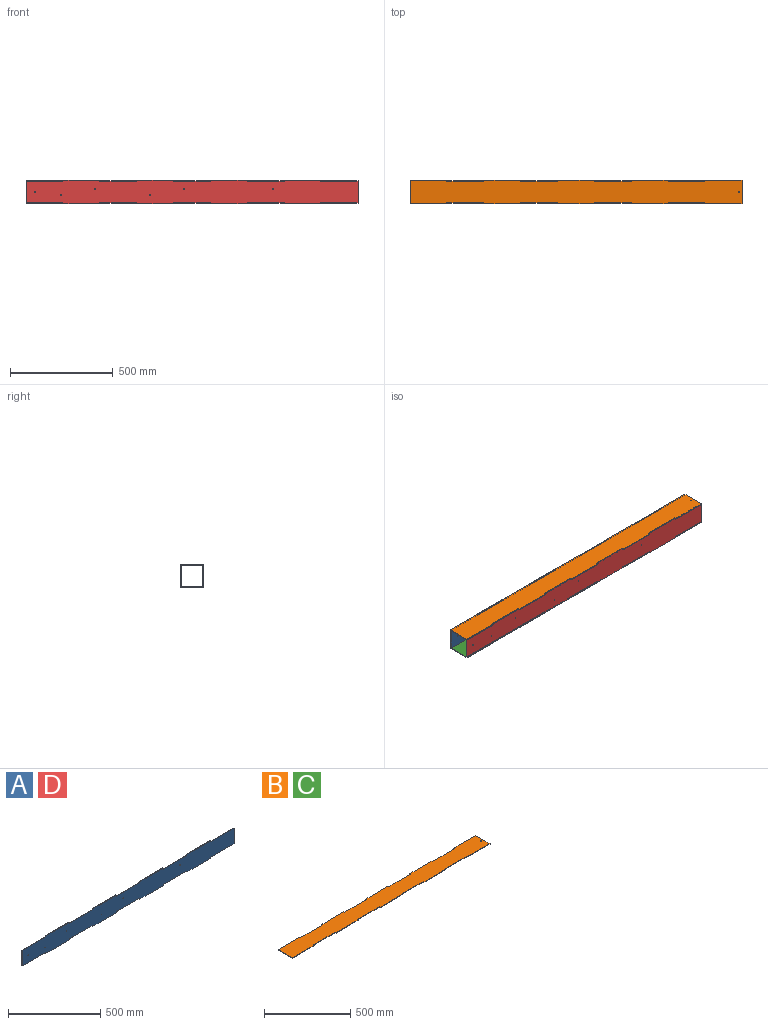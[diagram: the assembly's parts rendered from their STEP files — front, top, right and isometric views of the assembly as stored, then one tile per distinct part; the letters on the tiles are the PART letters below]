
ASSEMBLY  parts=4 mates=9
PART A: 44 faces, bbox 1619.3x3.2x115.9 mm
  f0: plane 103.19x3.18mm, normal (-1,0,0), area 327.6mm2, adj f1,f40,f42,f43
  f1: plane 179.83x3.18mm, normal (0,0,-1), area 571mm2, adj f0,f2,f42,f43
  f2: plane 6.35x3.18mm, normal (-1,0,0), area 20.2mm2, adj f1,f3,f42,f43
  f3: plane 179.83x3.18mm, normal (0,0,-1), area 571mm2, adj f2,f4,f42,f43
  f4: plane 6.35x3.18mm, normal (1,0,0), area 20.2mm2, adj f3,f5,f42,f43
  f5: plane 179.83x3.18mm, normal (0,0,-1), area 571mm2, adj f4,f6,f42,f43
  f6: plane 6.35x3.18mm, normal (-1,0,0), area 20.2mm2, adj f5,f7,f42,f43
  f7: plane 179.83x3.18mm, normal (0,0,-1), area 571mm2, adj f6,f8,f42,f43
  f8: plane 6.35x3.18mm, normal (1,0,0), area 20.2mm2, adj f7,f9,f42,f43
  f9: plane 179.83x3.18mm, normal (0,0,-1), area 571mm2, adj f8,f10,f42,f43
  f10: plane 6.35x3.18mm, normal (-1,0,0), area 20.2mm2, adj f9,f11,f42,f43
  f11: plane 179.83x3.18mm, normal (0,0,-1), area 571mm2, adj f10,f12,f42,f43
  f12: plane 6.35x3.18mm, normal (1,0,0), area 20.2mm2, adj f11,f13,f42,f43
  f13: plane 179.83x3.18mm, normal (0,0,-1), area 571mm2, adj f12,f14,f42,f43
  f14: plane 6.35x3.18mm, normal (-1,0,0), area 20.2mm2, adj f13,f15,f42,f43
  f15: plane 179.83x3.18mm, normal (0,0,-1), area 571mm2, adj f14,f16,f42,f43
  f16: plane 6.35x3.18mm, normal (1,0,0), area 20.2mm2, adj f15,f17,f42,f43
  f17: plane 180.59x3.18mm, normal (0,0,-1), area 573.4mm2, adj f16,f18,f42,f43
  f18: plane 103.19x3.18mm, normal (1,0,0), area 327.6mm2, adj f17,f19,f42,f43
  f19: plane 180.59x3.18mm, normal (0,0,1), area 573.4mm2, adj f18,f20,f42,f43
  f20: plane 6.35x3.18mm, normal (1,0,0), area 20.2mm2, adj f19,f21,f42,f43
  f21: plane 179.83x3.18mm, normal (0,0,1), area 571mm2, adj f20,f22,f42,f43
  f22: plane 6.35x3.18mm, normal (-1,0,0), area 20.2mm2, adj f21,f23,f42,f43
  f23: plane 179.83x3.18mm, normal (0,0,1), area 571mm2, adj f22,f24,f42,f43
  f24: plane 6.35x3.18mm, normal (1,0,0), area 20.2mm2, adj f23,f25,f42,f43
  f25: plane 179.83x3.18mm, normal (0,0,1), area 571mm2, adj f24,f26,f42,f43
  f26: plane 6.35x3.18mm, normal (-1,0,0), area 20.2mm2, adj f25,f27,f42,f43
  f27: plane 179.83x3.18mm, normal (0,0,1), area 571mm2, adj f26,f28,f42,f43
  f28: plane 6.35x3.18mm, normal (1,0,0), area 20.2mm2, adj f27,f29,f42,f43
  f29: plane 179.83x3.18mm, normal (0,0,1), area 571mm2, adj f28,f30,f42,f43
  f30: plane 6.35x3.18mm, normal (-1,0,0), area 20.2mm2, adj f29,f31,f42,f43
  f31: plane 179.83x3.18mm, normal (0,0,1), area 571mm2, adj f30,f32,f42,f43
  f32: plane 6.35x3.18mm, normal (1,0,0), area 20.2mm2, adj f31,f33,f42,f43
  f33: plane 179.83x3.18mm, normal (0,0,1), area 571mm2, adj f32,f34,f42,f43
  f34: plane 6.35x3.18mm, normal (-1,0,0), area 20.2mm2, adj f33,f40,f42,f43
  f35: cylinder r=2.39mm len=4.78mm, axis (0,1,0), area 47.6mm2, adj f42,f43
  f36: cylinder r=2.39mm len=4.78mm, axis (0,1,0), area 47.6mm2, adj f42,f43
  f37: cylinder r=2.39mm len=4.78mm, axis (0,1,0), area 47.6mm2, adj f42,f43
  f38: cylinder r=2.39mm len=4.78mm, axis (0,1,0), area 47.6mm2, adj f42,f43
  f39: cylinder r=2.39mm len=4.78mm, axis (0,1,0), area 47.6mm2, adj f42,f43
  f40: plane 179.83x3.18mm, normal (0,0,1), area 571mm2, adj f0,f34,f42,f43
  f41: cylinder r=2.39mm len=4.78mm, axis (0,1,0), area 47.6mm2, adj f42,f43
  f42: plane 1619.25x115.89mm, normal (0,-1,0), area 176114.4mm2, adj f0,f1,f2,f3,f4,f5,f6,f7
  f43: plane 1619.25x115.89mm, normal (0,1,0), area 176114.4mm2, adj f0,f1,f2,f3,f4,f5,f6,f7
PART B: 39 faces, bbox 1619.3x115.9x3.2 mm
  f0: plane 115.89x3.18mm, normal (-1,0,0), area 367.9mm2, adj f1,f36,f37,f38
  f1: plane 179.83x3.18mm, normal (0,-1,0), area 571mm2, adj f0,f2,f37,f38
  f2: plane 6.35x3.18mm, normal (1,0,0), area 20.2mm2, adj f1,f3,f37,f38
  f3: plane 179.83x3.18mm, normal (0,-1,0), area 571mm2, adj f2,f4,f37,f38
  f4: plane 6.35x3.18mm, normal (-1,0,0), area 20.2mm2, adj f3,f5,f37,f38
  f5: plane 179.83x3.18mm, normal (0,-1,0), area 571mm2, adj f4,f6,f37,f38
  f6: plane 6.35x3.18mm, normal (1,0,0), area 20.2mm2, adj f5,f7,f37,f38
  f7: plane 179.83x3.18mm, normal (0,-1,0), area 571mm2, adj f6,f8,f37,f38
  f8: plane 6.35x3.18mm, normal (-1,0,0), area 20.2mm2, adj f7,f9,f37,f38
  f9: plane 179.83x3.18mm, normal (0,-1,0), area 571mm2, adj f8,f10,f37,f38
  f10: plane 6.35x3.18mm, normal (1,0,0), area 20.2mm2, adj f9,f11,f37,f38
  f11: plane 179.83x3.18mm, normal (0,-1,0), area 571mm2, adj f10,f12,f37,f38
  f12: plane 6.35x3.18mm, normal (-1,0,0), area 20.2mm2, adj f11,f13,f37,f38
  f13: plane 179.83x3.18mm, normal (0,-1,0), area 571mm2, adj f12,f14,f37,f38
  f14: plane 6.35x3.18mm, normal (1,0,0), area 20.2mm2, adj f13,f15,f37,f38
  f15: plane 179.83x3.18mm, normal (0,-1,0), area 571mm2, adj f14,f16,f37,f38
  f16: plane 6.35x3.18mm, normal (-1,0,0), area 20.2mm2, adj f15,f17,f37,f38
  f17: plane 180.59x3.18mm, normal (0,-1,0), area 573.4mm2, adj f16,f18,f37,f38
  f18: plane 115.89x3.18mm, normal (1,0,0), area 367.9mm2, adj f17,f19,f37,f38
  f19: plane 180.59x3.18mm, normal (0,1,0), area 573.4mm2, adj f18,f20,f37,f38
  f20: plane 6.35x3.18mm, normal (-1,0,0), area 20.2mm2, adj f19,f21,f37,f38
  f21: plane 179.83x3.18mm, normal (0,1,0), area 571mm2, adj f20,f22,f37,f38
  f22: plane 6.35x3.18mm, normal (1,0,0), area 20.2mm2, adj f21,f23,f37,f38
  f23: plane 179.83x3.18mm, normal (0,1,0), area 571mm2, adj f22,f24,f37,f38
  f24: plane 6.35x3.18mm, normal (-1,0,0), area 20.2mm2, adj f23,f25,f37,f38
  f25: plane 179.83x3.18mm, normal (0,1,0), area 571mm2, adj f24,f26,f37,f38
  f26: plane 6.35x3.18mm, normal (1,0,0), area 20.2mm2, adj f25,f27,f37,f38
  f27: plane 179.83x3.18mm, normal (0,1,0), area 571mm2, adj f26,f28,f37,f38
  f28: plane 6.35x3.18mm, normal (-1,0,0), area 20.2mm2, adj f27,f29,f37,f38
  f29: plane 179.83x3.18mm, normal (0,1,0), area 571mm2, adj f28,f30,f37,f38
  f30: plane 6.35x3.18mm, normal (1,0,0), area 20.2mm2, adj f29,f31,f37,f38
  f31: plane 179.83x3.18mm, normal (0,1,0), area 571mm2, adj f30,f32,f37,f38
  f32: plane 6.35x3.18mm, normal (-1,0,0), area 20.2mm2, adj f31,f33,f37,f38
  f33: plane 179.83x3.18mm, normal (0,1,0), area 571mm2, adj f32,f34,f37,f38
  f34: plane 6.35x3.18mm, normal (1,0,0), area 20.2mm2, adj f33,f36,f37,f38
  f35: cylinder r=2.39mm len=4.78mm, axis (0,0,-1), area 47.6mm2, adj f37,f38
  f36: plane 179.83x3.18mm, normal (0,1,0), area 571mm2, adj f0,f34,f37,f38
  f37: plane 1619.25x115.89mm, normal (0,0,1), area 178497.5mm2, adj f0,f1,f2,f3,f4,f5,f6,f7
  f38: plane 1619.25x115.89mm, normal (0,0,-1), area 178497.5mm2, adj f0,f1,f2,f3,f4,f5,f6,f7
PART C: same geometry as B
PART D: same geometry as A
PLACE A t=(66.07,581.85,-176.5)mm
PLACE B t=(66.07,443.11,-73.31)mm
PLACE C t=(66.07,443.11,-179.67)mm
PLACE D t=(66.07,475.49,-176.5)mm
MATE planar B.f33 <-> A.f42  axis (0,1,0) through (335.82,578.67,-71.72)mm
MATE planar B.f0 <-> C.f0  axis (-1,0,0) through (66.07,527.08,-71.72)mm
MATE planar A.f1 <-> C.f37  axis (0,0,-1) through (155.99,580.26,-176.5)mm
MATE planar B.f3 <-> D.f43  axis (0,-1,0) through (335.82,475.49,-71.72)mm
MATE planar A.f42 <-> C.f33  axis (0,-1,0) through (425.74,578.67,-182.85)mm
MATE planar A.f27 <-> B.f38  axis (0,0,1) through (875.32,580.26,-73.31)mm
MATE planar D.f40 <-> B.f38  axis (0,0,1) through (155.99,473.9,-73.31)mm
MATE planar A.f0 <-> B.f0  axis (-1,0,0) through (66.07,580.26,-124.9)mm
MATE planar D.f0 <-> A.f0  axis (-1,0,0) through (66.07,473.9,-124.9)mm
